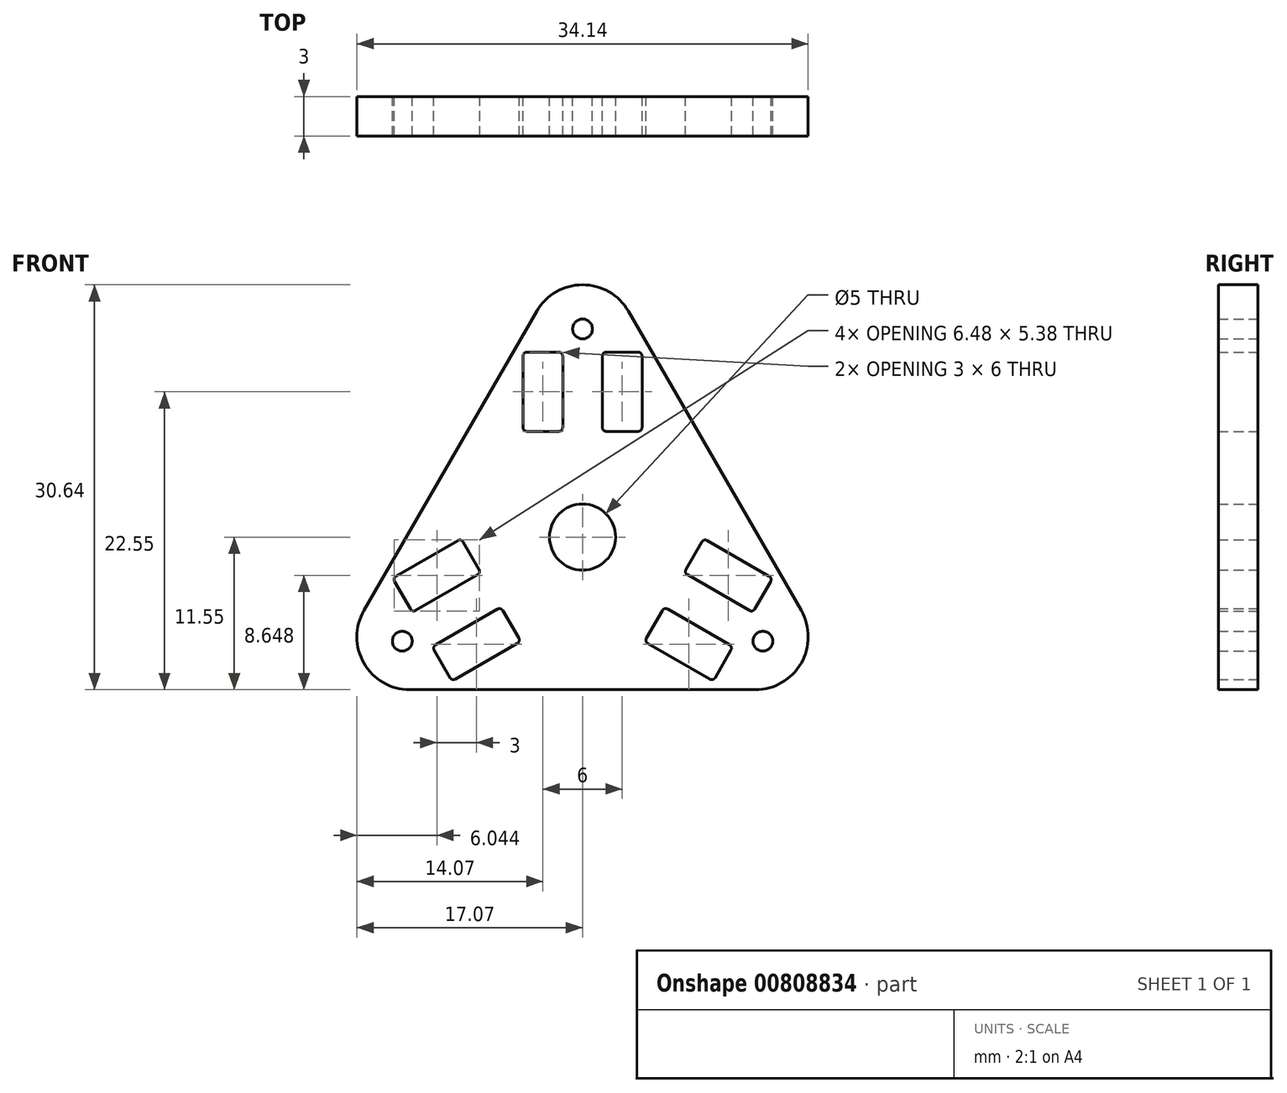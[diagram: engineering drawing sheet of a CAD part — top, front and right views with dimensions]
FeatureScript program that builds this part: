
annotation { "Feature Type Name" : "Feature", "Feature Type Description" : "" }
export const myFeature = defineFeature(function(context is Context, id is Id, definition is map)
    precondition{}
    {
        {
            var Q0;
            Q0=qCreatedBy(makeId("Front.planeOp"),FACE);
            var sketch = newSketch(context, id + "F0", { "sketchPlane" : qUnion([Q0])});
            skCircle(sketch, "E0.cCircle", {"center": v(0, 0) * mm, "radius": 11.55 * mm, "construction": true});
            skLineSegment(sketch, "E0.0", {"start": v(3.46, 17.1) * mm, "end": v(16.54, -5.55) * mm});
            skLineSegment(sketch, "E0.1", {"start": v(13.07, -11.55) * mm, "end": v(-13.07, -11.55) * mm});
            skLineSegment(sketch, "E0.2", {"start": v(-16.54, -5.55) * mm, "end": v(-3.46, 17.1) * mm});
            skPoint(sketch, "E0.0.midPoint", {"position": v(10, 5.77) * mm});
            skCircle(sketch, "E1", {"center": v(0, 0) * mm, "radius": 2.5 * mm});
            skLineSegment(sketch, "E2.bottom", {"start": v(-1.8, 8) * mm, "end": v(-4.2, 8) * mm});
            skLineSegment(sketch, "E2.top", {"start": v(-1.8, 14) * mm, "end": v(-4.2, 14) * mm});
            skLineSegment(sketch, "E2.left", {"start": v(-1.5, 8.3) * mm, "end": v(-1.5, 13.7) * mm});
            skLineSegment(sketch, "E2.right", {"start": v(-4.5, 8.3) * mm, "end": v(-4.5, 13.7) * mm});
            skPoint(sketch, "E2.middle", {"position": v(-3, 11) * mm});
            skLineSegment(sketch, "E3.bottom", {"start": v(4.2, 8) * mm, "end": v(1.8, 8) * mm});
            skLineSegment(sketch, "E3.top", {"start": v(4.2, 14) * mm, "end": v(1.8, 14) * mm});
            skLineSegment(sketch, "E3.left", {"start": v(4.5, 8.3) * mm, "end": v(4.5, 13.7) * mm});
            skLineSegment(sketch, "E3.right", {"start": v(1.5, 8.3) * mm, "end": v(1.5, 13.7) * mm});
            skPoint(sketch, "E3.middle", {"position": v(3, 11) * mm});
            skPoint(sketch, "E4.visualSharp", {"position": v(0, 23.1) * mm});
            skArc(sketch, "E4.filletArc", {"start": v(3.46, 17.1) * mm, "mid": v(0, 19.1) * mm, "end": v(-3.46, 17.1) * mm});
            skLineSegment(sketch, "E5.1.0", {"start": v(-9.03, -0.36) * mm, "end": v(-7.83, -2.44) * mm});
            skLineSegment(sketch, "E5.1.1", {"start": v(-14.22, -3.36) * mm, "end": v(-13.02, -5.44) * mm});
            skLineSegment(sketch, "E5.1.2", {"start": v(-9.44, -0.25) * mm, "end": v(-14.11, -2.95) * mm});
            skLineSegment(sketch, "E5.2.0", {"start": v(4.83, -7.64) * mm, "end": v(6.03, -5.56) * mm});
            skLineSegment(sketch, "E5.2.1", {"start": v(10.02, -10.64) * mm, "end": v(11.22, -8.56) * mm});
            skLineSegment(sketch, "E5.2.2", {"start": v(4.94, -8.05) * mm, "end": v(9.61, -10.75) * mm});
            skLineSegment(sketch, "E6.1.0", {"start": v(-6.44, -5.45) * mm, "end": v(-11.11, -8.15) * mm});
            skLineSegment(sketch, "E6.1.1", {"start": v(-6.03, -5.56) * mm, "end": v(-4.83, -7.64) * mm});
            skLineSegment(sketch, "E6.1.2", {"start": v(-4.94, -8.05) * mm, "end": v(-9.61, -10.75) * mm});
            skLineSegment(sketch, "E6.1.3", {"start": v(-11.22, -8.56) * mm, "end": v(-10.02, -10.64) * mm});
            skLineSegment(sketch, "E6.1.4", {"start": v(-7.94, -2.85) * mm, "end": v(-12.61, -5.55) * mm});
            skLineSegment(sketch, "E6.2.0", {"start": v(7.94, -2.85) * mm, "end": v(12.61, -5.55) * mm});
            skLineSegment(sketch, "E6.2.1", {"start": v(7.83, -2.44) * mm, "end": v(9.03, -0.36) * mm});
            skLineSegment(sketch, "E6.2.2", {"start": v(9.44, -0.25) * mm, "end": v(14.11, -2.95) * mm});
            skLineSegment(sketch, "E6.2.3", {"start": v(13.02, -5.44) * mm, "end": v(14.22, -3.36) * mm});
            skLineSegment(sketch, "E6.2.4", {"start": v(6.44, -5.45) * mm, "end": v(11.11, -8.15) * mm});
            skPoint(sketch, "E7.visualSharp", {"position": v(20, -11.55) * mm});
            skArc(sketch, "E7.filletArc", {"start": v(13.07, -11.55) * mm, "mid": v(16.54, -9.55) * mm, "end": v(16.54, -5.55) * mm});
            skPoint(sketch, "E8.visualSharp", {"position": v(-20, -11.55) * mm});
            skArc(sketch, "E8.filletArc", {"start": v(-16.54, -5.55) * mm, "mid": v(-16.54, -9.55) * mm, "end": v(-13.07, -11.55) * mm});
            skPoint(sketch, "E9.visualSharp", {"position": v(-4.5, 14) * mm});
            skArc(sketch, "E9.filletArc", {"start": v(-4.2, 14) * mm, "mid": v(-4.41, 13.91) * mm, "end": v(-4.5, 13.7) * mm});
            skPoint(sketch, "E10.visualSharp", {"position": v(-1.5, 14) * mm});
            skArc(sketch, "E10.filletArc", {"start": v(-1.5, 13.7) * mm, "mid": v(-1.59, 13.91) * mm, "end": v(-1.8, 14) * mm});
            skPoint(sketch, "E11.visualSharp", {"position": v(-1.5, 8) * mm});
            skArc(sketch, "E11.filletArc", {"start": v(-1.8, 8) * mm, "mid": v(-1.59, 8.09) * mm, "end": v(-1.5, 8.3) * mm});
            skPoint(sketch, "E12.visualSharp", {"position": v(-4.5, 8) * mm});
            skArc(sketch, "E12.filletArc", {"start": v(-4.5, 8.3) * mm, "mid": v(-4.41, 8.09) * mm, "end": v(-4.2, 8) * mm});
            skPoint(sketch, "E13.visualSharp", {"position": v(1.5, 14) * mm});
            skArc(sketch, "E13.filletArc", {"start": v(1.8, 14) * mm, "mid": v(1.59, 13.91) * mm, "end": v(1.5, 13.7) * mm});
            skPoint(sketch, "E14.visualSharp", {"position": v(4.5, 14) * mm});
            skArc(sketch, "E14.filletArc", {"start": v(4.5, 13.7) * mm, "mid": v(4.41, 13.91) * mm, "end": v(4.2, 14) * mm});
            skPoint(sketch, "E15.visualSharp", {"position": v(4.5, 8) * mm});
            skArc(sketch, "E15.filletArc", {"start": v(4.2, 8) * mm, "mid": v(4.41, 8.09) * mm, "end": v(4.5, 8.3) * mm});
            skPoint(sketch, "E16.visualSharp", {"position": v(1.5, 8) * mm});
            skArc(sketch, "E16.filletArc", {"start": v(1.5, 8.3) * mm, "mid": v(1.59, 8.09) * mm, "end": v(1.8, 8) * mm});
            skPoint(sketch, "E17.visualSharp", {"position": v(-7.68, -2.7) * mm});
            skArc(sketch, "E17.filletArc", {"start": v(-7.94, -2.85) * mm, "mid": v(-7.8, -2.67) * mm, "end": v(-7.83, -2.44) * mm});
            skPoint(sketch, "E18.visualSharp", {"position": v(-12.87, -5.7) * mm});
            skArc(sketch, "E18.filletArc", {"start": v(-13.02, -5.44) * mm, "mid": v(-12.84, -5.58) * mm, "end": v(-12.61, -5.55) * mm});
            skPoint(sketch, "E19.visualSharp", {"position": v(-11.37, -8.3) * mm});
            skArc(sketch, "E19.filletArc", {"start": v(-11.11, -8.15) * mm, "mid": v(-11.25, -8.33) * mm, "end": v(-11.22, -8.56) * mm});
            skPoint(sketch, "E20.visualSharp", {"position": v(-14.37, -3.1) * mm});
            skArc(sketch, "E20.filletArc", {"start": v(-14.11, -2.95) * mm, "mid": v(-14.25, -3.14) * mm, "end": v(-14.22, -3.36) * mm});
            skPoint(sketch, "E21.visualSharp", {"position": v(-9.18, -0.1) * mm});
            skArc(sketch, "E21.filletArc", {"start": v(-9.03, -0.36) * mm, "mid": v(-9.21, -0.22) * mm, "end": v(-9.44, -0.25) * mm});
            skPoint(sketch, "E22.visualSharp", {"position": v(-4.68, -7.9) * mm});
            skArc(sketch, "E22.filletArc", {"start": v(-4.94, -8.05) * mm, "mid": v(-4.8, -7.86) * mm, "end": v(-4.83, -7.64) * mm});
            skPoint(sketch, "E23.visualSharp", {"position": v(-6.18, -5.3) * mm});
            skArc(sketch, "E23.filletArc", {"start": v(-6.03, -5.56) * mm, "mid": v(-6.21, -5.42) * mm, "end": v(-6.44, -5.45) * mm});
            skPoint(sketch, "E24.visualSharp", {"position": v(-9.87, -10.9) * mm});
            skArc(sketch, "E24.filletArc", {"start": v(-10.02, -10.64) * mm, "mid": v(-9.84, -10.78) * mm, "end": v(-9.61, -10.75) * mm});
            skPoint(sketch, "E25.visualSharp", {"position": v(6.18, -5.3) * mm});
            skArc(sketch, "E25.filletArc", {"start": v(6.44, -5.45) * mm, "mid": v(6.21, -5.42) * mm, "end": v(6.03, -5.56) * mm});
            skPoint(sketch, "E26.visualSharp", {"position": v(4.68, -7.9) * mm});
            skArc(sketch, "E26.filletArc", {"start": v(4.83, -7.64) * mm, "mid": v(4.8, -7.86) * mm, "end": v(4.94, -8.05) * mm});
            skPoint(sketch, "E27.visualSharp", {"position": v(11.37, -8.3) * mm});
            skArc(sketch, "E27.filletArc", {"start": v(11.22, -8.56) * mm, "mid": v(11.25, -8.33) * mm, "end": v(11.11, -8.15) * mm});
            skPoint(sketch, "E28.visualSharp", {"position": v(12.87, -5.7) * mm});
            skArc(sketch, "E28.filletArc", {"start": v(12.61, -5.55) * mm, "mid": v(12.84, -5.58) * mm, "end": v(13.02, -5.44) * mm});
            skPoint(sketch, "E29.visualSharp", {"position": v(14.37, -3.1) * mm});
            skArc(sketch, "E29.filletArc", {"start": v(14.22, -3.36) * mm, "mid": v(14.25, -3.14) * mm, "end": v(14.11, -2.95) * mm});
            skPoint(sketch, "E30.visualSharp", {"position": v(7.68, -2.7) * mm});
            skArc(sketch, "E30.filletArc", {"start": v(7.83, -2.44) * mm, "mid": v(7.8, -2.67) * mm, "end": v(7.94, -2.85) * mm});
            skPoint(sketch, "E31.visualSharp", {"position": v(9.18, -0.1) * mm});
            skArc(sketch, "E31.filletArc", {"start": v(9.44, -0.25) * mm, "mid": v(9.21, -0.22) * mm, "end": v(9.03, -0.36) * mm});
            skPoint(sketch, "E32.visualSharp", {"position": v(9.87, -10.9) * mm});
            skArc(sketch, "E32.filletArc", {"start": v(9.61, -10.75) * mm, "mid": v(9.84, -10.78) * mm, "end": v(10.02, -10.64) * mm});
            skSolve(sketch);
        }
        {
            var Q0;
            Q0=makeQuery(id+"F0.imprint","IMPRINT",FACE,{"disambiguationData":[TD([[makeQuery(id+"F0.imprint","IMPRINT",EDGE,{"derivedFrom":sQuery(id+"F0.wireOp",EDGE,"E1")}),-1.0]])]});
            extrude(context, id + "F1", {"entities" : qUnion([Q0]), "depth" : 3 * mm, "offsetDistance" : 25 * mm});
        }
        {
            var Q0;
            Q0=makeQuery(id+"F1.opExtrude","CAP_FACE",FACE,{"disambiguationData":[OSD([sQuery(id+"F0.wireOp",EDGE,"E0.0"),sQuery(id+"F0.wireOp",EDGE,"E0.1"),sQuery(id+"F0.wireOp",EDGE,"E0.2"),sQuery(id+"F0.wireOp",EDGE,"E1"),sQuery(id+"F0.wireOp",EDGE,"E2.bottom"),sQuery(id+"F0.wireOp",EDGE,"E2.top"),sQuery(id+"F0.wireOp",EDGE,"E2.left"),sQuery(id+"F0.wireOp",EDGE,"E2.right"),sQuery(id+"F0.wireOp",EDGE,"E3.bottom"),sQuery(id+"F0.wireOp",EDGE,"E3.top"),sQuery(id+"F0.wireOp",EDGE,"E3.left"),sQuery(id+"F0.wireOp",EDGE,"E3.right"),sQuery(id+"F0.wireOp",EDGE,"E4.filletArc"),sQuery(id+"F0.wireOp",EDGE,"E5.1.0"),sQuery(id+"F0.wireOp",EDGE,"E5.1.1"),sQuery(id+"F0.wireOp",EDGE,"E5.1.2"),sQuery(id+"F0.wireOp",EDGE,"E5.2.0"),sQuery(id+"F0.wireOp",EDGE,"E5.2.1"),sQuery(id+"F0.wireOp",EDGE,"E5.2.2"),sQuery(id+"F0.wireOp",EDGE,"E6.1.0"),sQuery(id+"F0.wireOp",EDGE,"E6.1.1"),sQuery(id+"F0.wireOp",EDGE,"E6.1.2"),sQuery(id+"F0.wireOp",EDGE,"E6.1.3"),sQuery(id+"F0.wireOp",EDGE,"E6.1.4"),sQuery(id+"F0.wireOp",EDGE,"E6.2.0"),sQuery(id+"F0.wireOp",EDGE,"E6.2.1"),sQuery(id+"F0.wireOp",EDGE,"E6.2.2"),sQuery(id+"F0.wireOp",EDGE,"E6.2.3"),sQuery(id+"F0.wireOp",EDGE,"E6.2.4"),sQuery(id+"F0.wireOp",EDGE,"E7.filletArc"),sQuery(id+"F0.wireOp",EDGE,"E8.filletArc")])],"isStart":true});
            var sketch = newSketch(context, id + "F2", { "sketchPlane" : qUnion([Q0])});
            skCircle(sketch, "E33", {"center": v(0, 15.75) * mm, "radius": 0.75 * mm});
            skCircle(sketch, "E34.1.0", {"center": v(-13.64, -7.87) * mm, "radius": 0.75 * mm});
            skCircle(sketch, "E34.2.0", {"center": v(13.64, -7.87) * mm, "radius": 0.75 * mm});
            skPoint(sketch, "E34.center", {"position": v(0, 0) * mm});
            skSolve(sketch);
        }
        {
            var Q0;
            Q0=qSketchRegion(id+"F2",true);
            extrude(context, id + "F3", {"entities" : qUnion([Q0]), "operationType" : NewBodyOperationType.REMOVE, "oppositeDirection" : true, "depth" : 25 * mm, "offsetDistance" : 25 * mm});
        }
    });
